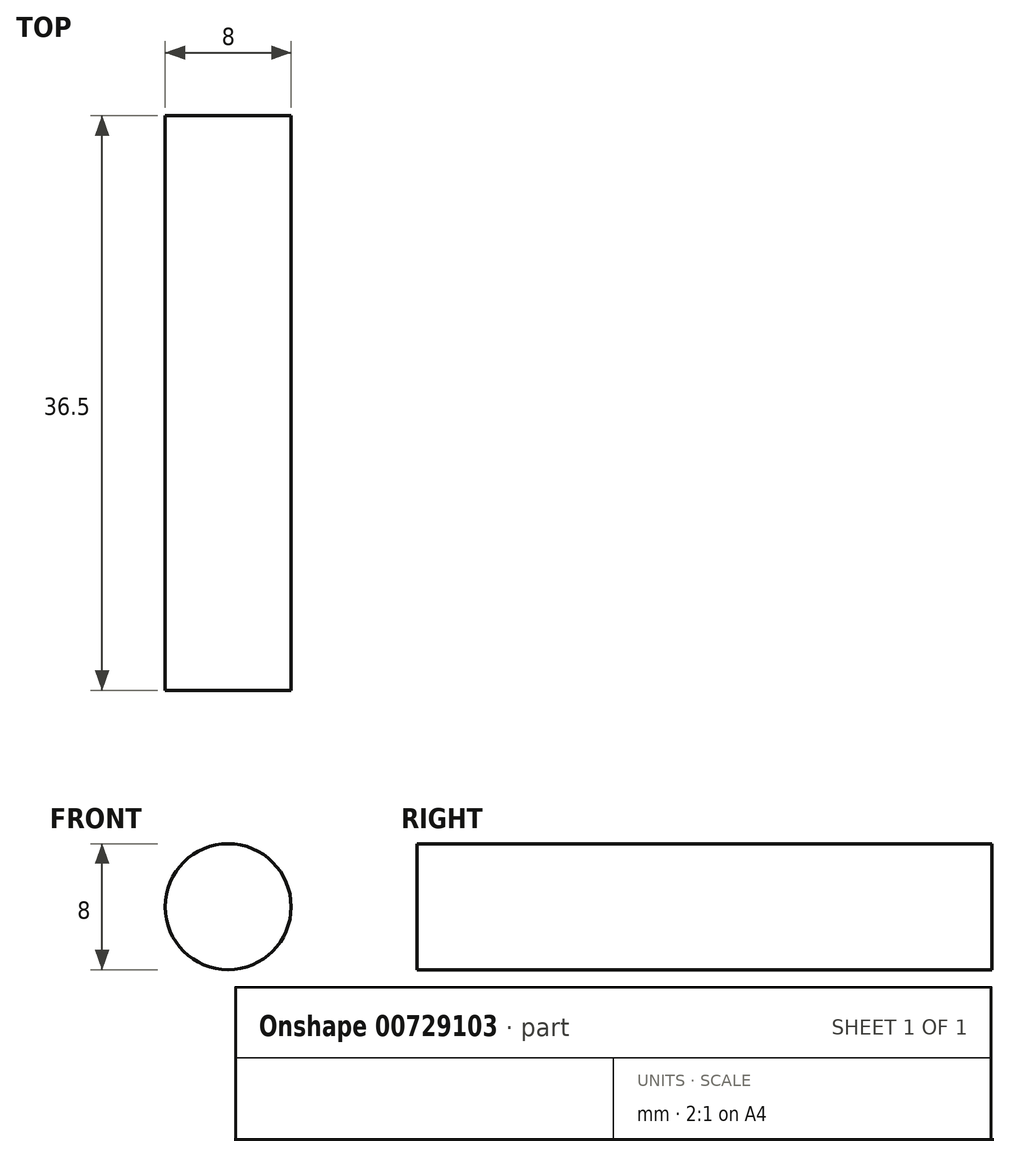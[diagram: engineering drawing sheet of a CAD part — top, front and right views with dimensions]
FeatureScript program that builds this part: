
annotation { "Feature Type Name" : "Feature", "Feature Type Description" : "" }
export const myFeature = defineFeature(function(context is Context, id is Id, definition is map)
    precondition{}
    {
        {
            var Q0;
            Q0=qCreatedBy(makeId("Front.planeOp"), FACE);
            var sketch = newSketch(context, id + "F0", { "sketchPlane" : qUnion([Q0])});
            skCircle(sketch, "E0", {"center": v(42.45, -40.6) * mm, "radius": 4 * mm});
            skSolve(sketch);
        }
        {
            var Q0;
            Q0 = qSketchRegion(id + "F0", true);
            extrude(context, id + "F1", {"entities" : qUnion([Q0]), "depth" : 36.5 * mm, "offsetDistance" : 25 * mm});
        }
    });
